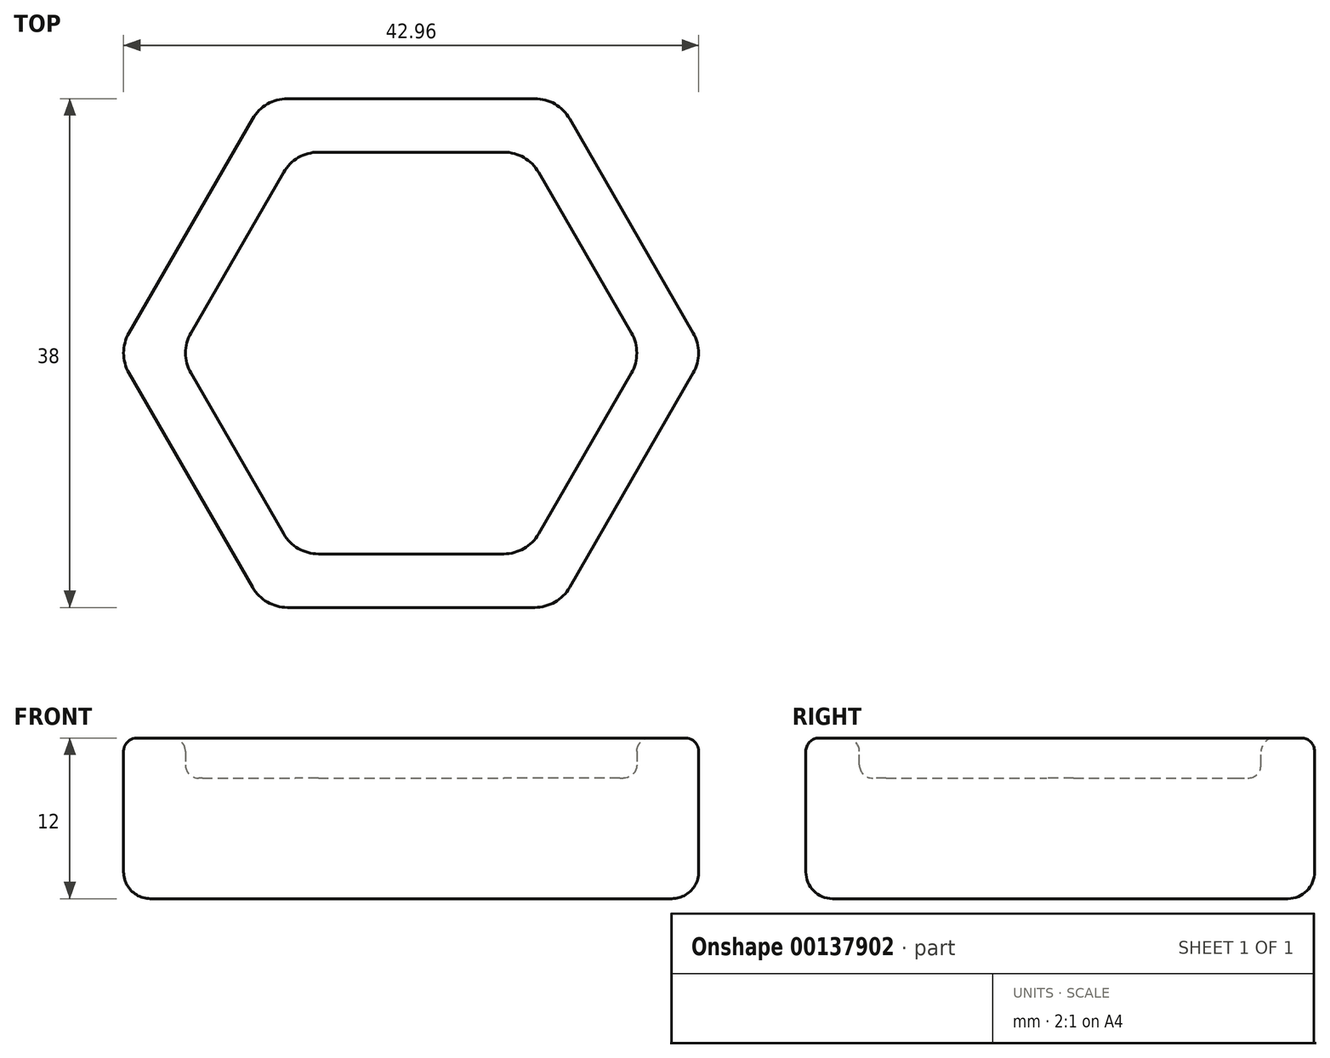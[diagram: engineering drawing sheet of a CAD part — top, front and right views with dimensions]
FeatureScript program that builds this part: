
annotation { "Feature Type Name" : "Feature", "Feature Type Description" : "" }
export const myFeature = defineFeature(function(context is Context, id is Id, definition is map)
    precondition{}
    {
        {
            var Q0;
            Q0=qCreatedBy(makeId("Top.planeOp"),FACE);
            var sketch = newSketch(context, id + "F0", { "sketchPlane" : qUnion([Q0])});
            skLineSegment(sketch, "E0", {"start": v(0, 0) * mm, "end": v(0, 19) * mm, "construction": true});
            skCircle(sketch, "E1.cCircle", {"center": v(0, 0) * mm, "radius": 19 * mm, "construction": true});
            skLineSegment(sketch, "E1.0", {"start": v(-10.97, 19) * mm, "end": v(10.97, 19) * mm});
            skLineSegment(sketch, "E1.1", {"start": v(10.97, 19) * mm, "end": v(21.94, 0) * mm});
            skLineSegment(sketch, "E1.2", {"start": v(21.94, 0) * mm, "end": v(10.97, -19) * mm});
            skLineSegment(sketch, "E1.3", {"start": v(10.97, -19) * mm, "end": v(-10.97, -19) * mm});
            skLineSegment(sketch, "E1.4", {"start": v(-10.97, -19) * mm, "end": v(-21.94, 0) * mm});
            skLineSegment(sketch, "E1.5", {"start": v(-21.94, 0) * mm, "end": v(-10.97, 19) * mm});
            skPoint(sketch, "E1.0.midPoint", {"position": v(0, 19) * mm});
            skSolve(sketch);
        }
        {
            var Q0;
            Q0=makeQuery(id+"F0.imprint","IMPRINT",FACE,{"disambiguationData":[TD([[makeQuery(id+"F0.imprint","IMPRINT",EDGE,{"derivedFrom":sQuery(id+"F0.wireOp",EDGE,"E1.0")}),-1.0]])]});
            extrude(context, id + "F1", {"entities" : qUnion([Q0]), "depth" : 12 * mm});
        }
        {
            var Q0;
            Q0=makeQuery(id+"F1.opExtrude","SWEPT_EDGE",EDGE,{"disambiguationData":[OSD([sQuery(id+"F0.wireOp",EDGE,"E1.3"),sQuery(id+"F0.wireOp",EDGE,"E1.4")])]});
            var Q1;
            Q1=makeQuery(id+"F1.opExtrude","SWEPT_EDGE",EDGE,{"disambiguationData":[OSD([sQuery(id+"F0.wireOp",EDGE,"E1.2"),sQuery(id+"F0.wireOp",EDGE,"E1.3")])]});
            var Q2;
            Q2=makeQuery(id+"F1.opExtrude","SWEPT_EDGE",EDGE,{"disambiguationData":[OSD([sQuery(id+"F0.wireOp",EDGE,"E1.1"),sQuery(id+"F0.wireOp",EDGE,"E1.2")])]});
            var Q3;
            Q3=makeQuery(id+"F1.opExtrude","SWEPT_EDGE",EDGE,{"disambiguationData":[OSD([sQuery(id+"F0.wireOp",EDGE,"E1.4"),sQuery(id+"F0.wireOp",EDGE,"E1.5")])]});
            var Q4;
            Q4=makeQuery(id+"F1.opExtrude","SWEPT_EDGE",EDGE,{"disambiguationData":[OSD([sQuery(id+"F0.wireOp",EDGE,"E1.0"),sQuery(id+"F0.wireOp",EDGE,"E1.5")])]});
            var Q5;
            Q5=makeQuery(id+"F1.opExtrude","SWEPT_EDGE",EDGE,{"disambiguationData":[OSD([sQuery(id+"F0.wireOp",EDGE,"E1.0"),sQuery(id+"F0.wireOp",EDGE,"E1.1")])]});
            fillet(context, id + "F2", {"entities" : qUnion([Q0, Q1, Q2, Q3, Q4, Q5]), "radius" : 3 * mm, "tangentPropagation" : true, "allowEdgeOverflow" : false});
        }
        {
            var Q0;
            Q0=makeQuery(id+"F1.opExtrude","CAP_FACE",FACE,{"disambiguationData":[OSD([sQuery(id+"F0.wireOp",EDGE,"E1.0"),sQuery(id+"F0.wireOp",EDGE,"E1.1"),sQuery(id+"F0.wireOp",EDGE,"E1.2"),sQuery(id+"F0.wireOp",EDGE,"E1.3"),sQuery(id+"F0.wireOp",EDGE,"E1.4"),sQuery(id+"F0.wireOp",EDGE,"E1.5")])],"isStart":true});
            fillet(context, id + "F3", {"entities" : qUnion([Q0]), "radius" : 2 * mm, "tangentPropagation" : true, "allowEdgeOverflow" : false});
        }
        {
            var Q0;
            Q0=makeQuery(id+"F1.opExtrude","CAP_FACE",FACE,{"disambiguationData":[OSD([sQuery(id+"F0.wireOp",EDGE,"E1.0"),sQuery(id+"F0.wireOp",EDGE,"E1.1"),sQuery(id+"F0.wireOp",EDGE,"E1.2"),sQuery(id+"F0.wireOp",EDGE,"E1.3"),sQuery(id+"F0.wireOp",EDGE,"E1.4"),sQuery(id+"F0.wireOp",EDGE,"E1.5")])],"isStart":false});
            var sketch = newSketch(context, id + "F4", { "sketchPlane" : qUnion([Q0])});
            skLineSegment(sketch, "E2", {"start": v(0, 0) * mm, "end": v(0, 15) * mm, "construction": true});
            skCircle(sketch, "E3.cCircle", {"center": v(0, 0) * mm, "radius": 15 * mm, "construction": true});
            skLineSegment(sketch, "E3.0", {"start": v(-8.66, 15) * mm, "end": v(8.66, 15) * mm});
            skLineSegment(sketch, "E3.1", {"start": v(8.66, 15) * mm, "end": v(17.32, 0) * mm});
            skLineSegment(sketch, "E3.2", {"start": v(17.32, 0) * mm, "end": v(8.66, -15) * mm});
            skLineSegment(sketch, "E3.3", {"start": v(8.66, -15) * mm, "end": v(-8.66, -15) * mm});
            skLineSegment(sketch, "E3.4", {"start": v(-8.66, -15) * mm, "end": v(-17.32, 0) * mm});
            skLineSegment(sketch, "E3.5", {"start": v(-17.32, 0) * mm, "end": v(-8.66, 15) * mm});
            skPoint(sketch, "E3.0.midPoint", {"position": v(0, 15) * mm});
            skSolve(sketch);
        }
        {
            var Q0;
            Q0 = qSketchRegion(id + "F4", true);
            extrude(context, id + "F5", {"entities" : qUnion([Q0]), "operationType" : NewBodyOperationType.REMOVE, "oppositeDirection" : true, "depth" : 3 * mm});
        }
        {
            var Q0;
            Q0=makeQuery(id+"F5.boolean.opBoolean","COPY",EDGE,{"derivedFrom":makeQuery(id+"F5.opExtrude","SWEPT_EDGE",EDGE,{"disambiguationData":[OSD([sQuery(id+"F4.wireOp",EDGE,"E3.0"),sQuery(id+"F4.wireOp",EDGE,"E3.5")])]})});
            var Q1;
            Q1=makeQuery(id+"F5.boolean.opBoolean","COPY",EDGE,{"derivedFrom":makeQuery(id+"F5.opExtrude","SWEPT_EDGE",EDGE,{"disambiguationData":[OSD([sQuery(id+"F4.wireOp",EDGE,"E3.0"),sQuery(id+"F4.wireOp",EDGE,"E3.1")])]})});
            var Q2;
            Q2=makeQuery(id+"F5.boolean.opBoolean","COPY",EDGE,{"derivedFrom":makeQuery(id+"F5.opExtrude","SWEPT_EDGE",EDGE,{"disambiguationData":[OSD([sQuery(id+"F4.wireOp",EDGE,"E3.1"),sQuery(id+"F4.wireOp",EDGE,"E3.2")])]})});
            var Q3;
            Q3=makeQuery(id+"F5.boolean.opBoolean","COPY",EDGE,{"derivedFrom":makeQuery(id+"F5.opExtrude","SWEPT_EDGE",EDGE,{"disambiguationData":[OSD([sQuery(id+"F4.wireOp",EDGE,"E3.4"),sQuery(id+"F4.wireOp",EDGE,"E3.5")])]})});
            var Q4;
            Q4=makeQuery(id+"F5.boolean.opBoolean","COPY",EDGE,{"derivedFrom":makeQuery(id+"F5.opExtrude","SWEPT_EDGE",EDGE,{"disambiguationData":[OSD([sQuery(id+"F4.wireOp",EDGE,"E3.3"),sQuery(id+"F4.wireOp",EDGE,"E3.4")])]})});
            var Q5;
            Q5=makeQuery(id+"F5.boolean.opBoolean","COPY",EDGE,{"derivedFrom":makeQuery(id+"F5.opExtrude","SWEPT_EDGE",EDGE,{"disambiguationData":[OSD([sQuery(id+"F4.wireOp",EDGE,"E3.2"),sQuery(id+"F4.wireOp",EDGE,"E3.3")])]})});
            fillet(context, id + "F6", {"entities" : qUnion([Q0, Q1, Q2, Q3, Q4, Q5]), "radius" : 3 * mm, "tangentPropagation" : true, "allowEdgeOverflow" : false});
        }
        {
            var Q0;
            Q0=makeQuery(id+"F1.opExtrude","CAP_FACE",FACE,{"disambiguationData":[OSD([sQuery(id+"F0.wireOp",EDGE,"E1.0"),sQuery(id+"F0.wireOp",EDGE,"E1.1"),sQuery(id+"F0.wireOp",EDGE,"E1.2"),sQuery(id+"F0.wireOp",EDGE,"E1.3"),sQuery(id+"F0.wireOp",EDGE,"E1.4"),sQuery(id+"F0.wireOp",EDGE,"E1.5")])],"isStart":false});
            fillet(context, id + "F7", {"entities" : qUnion([Q0]), "radius" : 1 * mm, "tangentPropagation" : true, "allowEdgeOverflow" : false});
        }
        {
            var Q0;
            Q0=makeQuery(id+"F5.boolean.opBoolean","COPY",FACE,{"derivedFrom":makeQuery(id+"F5.opExtrude","CAP_FACE",FACE,{"disambiguationData":[OSD([sQuery(id+"F4.wireOp",EDGE,"E3.0"),sQuery(id+"F4.wireOp",EDGE,"E3.1"),sQuery(id+"F4.wireOp",EDGE,"E3.2"),sQuery(id+"F4.wireOp",EDGE,"E3.3"),sQuery(id+"F4.wireOp",EDGE,"E3.4"),sQuery(id+"F4.wireOp",EDGE,"E3.5")])],"isStart":false})});
            fillet(context, id + "F8", {"entities" : qUnion([Q0]), "radius" : 1 * mm, "tangentPropagation" : true, "allowEdgeOverflow" : false});
        }
    });
